# Revit family: Door-TruStile_Doors-TS4240
name_source: partatom
category: Doors
revit_build: Autodesk Revit MEP 2014 (Build: 20140709_2115(x64)
units: mm (PartAtom-declared; Revit-internal decimal feet)

## types (5) — shared parameters
Assembly Code = C1020330
C Door Swing = 90.00°
Description = TruStile (TS) Series
Door Swing = 90.00°
Fire Rating = See Product Documentation Link for more information
Fire Rating Data = http://www.trustile.com
Frame Finish Material = Wood - TruStile - Doors - MDF
Frame Projection Ext. = 0' - 1"
Frame Projection Int. = 0' - 1"
Frame Width = 0' - 3"
Function = Interior
Glass Finish Material = Glass - TruStile - Doors - Clear
Green Data = http://www.trustile.com
Jamb Thickness = 0' - 1"
Keynote = 08 14 00
Manufacturer = TruStile Doors, LLC
Model = TS4240
Panel Finish Material = Wood - TruStile - Doors - MDF
Product Documentation Link = http://www.trustile.com
Product Page URL = http://www.trustile.com
Sticking Finish Material = Wood - TruStile - Doors - MDF
Stile Finish Material = Wood - TruStile - Doors - MDF
URL = http://www.trustile.com
Version = 2014 – v1.0a
Wall Closure = By host

## per-type parameters (varying)
| type | Door Thickness (1-3/4in, 1-3/8in, 2-1/4in) | Height | Rough Height | Rough Width | Thickness | Width |
| 30" x 80" | 0' - 1 3/4" | 6' - 8" | 7' - 0" | 3' - 2" | 0' - 1 3/4" | 2' - 6" |
| 32" x 84" | 0' - 1 3/8" | 7' - 0" | 7' - 4" | 3' - 4" | 0' - 1 3/8" | 2' - 8" |
| 34" x 88" | 0' - 1 3/8" | 7' - 4" | 7' - 8" | 3' - 6" | 0' - 1 3/8" | 2' - 10" |
| 36" x 92" | 0' - 1 3/8" | 7' - 8" | 8' - 0" | 3' - 8" | 0' - 1 3/8" | 3' - 0" |
| 42" x 96" | 0' - 1 3/8" | 8' - 0" | 8' - 4" | 4' - 2" | 0' - 1 3/8" | 3' - 6" |

## geometry (parser evidence)
native form markers: Blend x8, Sweep x13
no freeform markers — native parametric forms only
